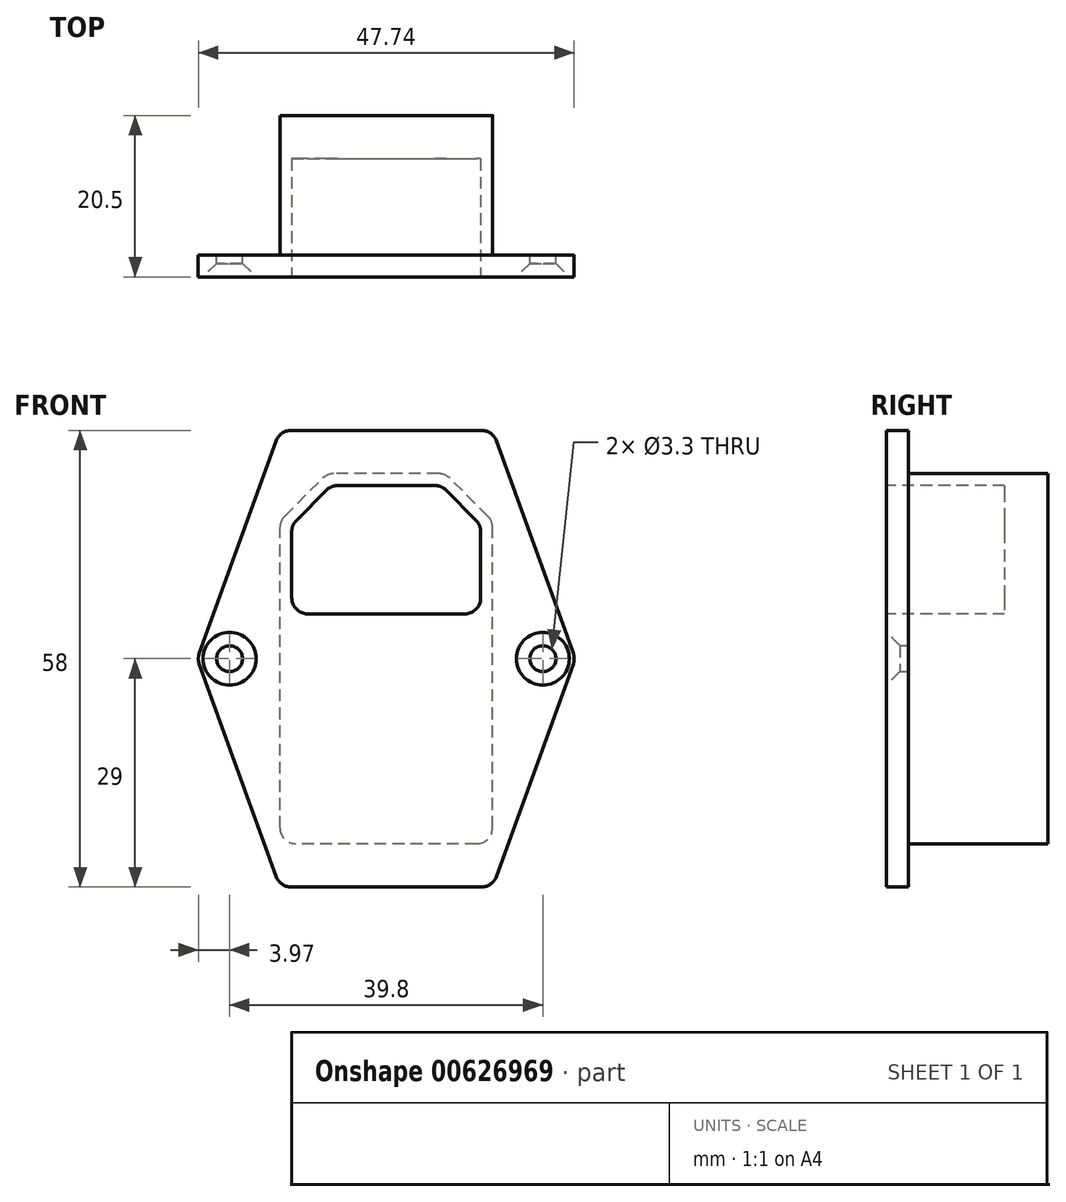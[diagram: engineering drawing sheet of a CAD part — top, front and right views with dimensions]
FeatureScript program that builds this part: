
annotation { "Feature Type Name" : "Feature", "Feature Type Description" : "" }
export const myFeature = defineFeature(function(context is Context, id is Id, definition is map)
    precondition{}
    {
        {
            var Q0;
            Q0=qCreatedBy(makeId("Front.planeOp"),FACE);
            var sketch = newSketch(context, id + "F0", { "sketchPlane" : qUnion([Q0])});
            skLineSegment(sketch, "E0", {"start": v(0, 0) * mm, "end": v(-13.5, 0) * mm});
            skLineSegment(sketch, "E1", {"start": v(-13.5, 0) * mm, "end": v(-13.5, 41) * mm});
            skLineSegment(sketch, "E2", {"start": v(-13.5, 41) * mm, "end": v(-7.5, 47) * mm});
            skLineSegment(sketch, "E3", {"start": v(-7.5, 47) * mm, "end": v(0, 47) * mm});
            skLineSegment(sketch, "E4", {"start": v(0, 47) * mm, "end": v(0, 0) * mm, "construction": true});
            skLineSegment(sketch, "E5", {"start": v(0, 23.5) * mm, "end": v(-24, 23.5) * mm, "construction": true});
            skLineSegment(sketch, "E6", {"start": v(0, 52.5) * mm, "end": v(-13.5, 52.5) * mm});
            skLineSegment(sketch, "E7", {"start": v(-13.5, 52.5) * mm, "end": v(-24, 23.5) * mm});
            skLineSegment(sketch, "E8.MirrorCS", {"start": v(0, -5.5) * mm, "end": v(-13.5, -5.5) * mm});
            skLineSegment(sketch, "E9.MirrorCS", {"start": v(-13.5, -5.5) * mm, "end": v(-24, 23.5) * mm});
            skLineSegment(sketch, "E10.MirrorCS", {"start": v(0, 52.5) * mm, "end": v(13.5, 52.5) * mm});
            skLineSegment(sketch, "E11.MirrorCS", {"start": v(13.5, 52.5) * mm, "end": v(24, 23.5) * mm});
            skLineSegment(sketch, "E12.MirrorCS", {"start": v(13.5, -5.5) * mm, "end": v(24, 23.5) * mm});
            skLineSegment(sketch, "E13.MirrorCS", {"start": v(0, -5.5) * mm, "end": v(13.5, -5.5) * mm});
            skLineSegment(sketch, "E14.MirrorCS", {"start": v(0, 0) * mm, "end": v(13.5, 0) * mm});
            skLineSegment(sketch, "E15.MirrorCS", {"start": v(7.5, 47) * mm, "end": v(0, 47) * mm});
            skLineSegment(sketch, "E16.MirrorCS", {"start": v(13.5, 41) * mm, "end": v(7.5, 47) * mm});
            skLineSegment(sketch, "E17.MirrorCS", {"start": v(13.5, 0) * mm, "end": v(13.5, 41) * mm});
            skSolve(sketch);
        }
        {
            var Q0;
            Q0=makeQuery(id+"F0.imprint","IMPRINT",FACE,{"disambiguationData":[TD([[makeQuery(id+"F0.imprint","IMPRINT",EDGE,{"derivedFrom":sQuery(id+"F0.wireOp",EDGE,"E0")}),1.0]])]});
            var Q1;
            Q1=makeQuery(id+"F0.imprint","IMPRINT",FACE,{"disambiguationData":[TD([[makeQuery(id+"F0.imprint","IMPRINT",EDGE,{"derivedFrom":sQuery(id+"F0.wireOp",EDGE,"E0")}),-1.0]])]});
            extrude(context, id + "F1", {"entities" : qUnion([Q0, Q1]), "depth" : 2.75 * mm, "offsetDistance" : 25 * mm});
        }
        {
            var Q0;
            Q0=makeQuery(id+"F0.imprint","IMPRINT",FACE,{"disambiguationData":[TD([[makeQuery(id+"F0.imprint","IMPRINT",EDGE,{"derivedFrom":sQuery(id+"F0.wireOp",EDGE,"E0")}),-1.0]])]});
            extrude(context, id + "F2", {"entities" : qUnion([Q0]), "operationType" : NewBodyOperationType.ADD, "oppositeDirection" : true, "depth" : (20.5 - 2.75) * mm, "offsetDistance" : 25 * mm});
        }
        {
            var Q0;
            Q0=makeQuery(id+"F1.opExtrude","CAP_FACE",FACE,{"disambiguationData":[OSD([sQuery(id+"F0.wireOp",EDGE,"E6"),sQuery(id+"F0.wireOp",EDGE,"E7"),sQuery(id+"F0.wireOp",EDGE,"E8.MirrorCS"),sQuery(id+"F0.wireOp",EDGE,"E9.MirrorCS"),sQuery(id+"F0.wireOp",EDGE,"E10.MirrorCS"),sQuery(id+"F0.wireOp",EDGE,"E11.MirrorCS"),sQuery(id+"F0.wireOp",EDGE,"E12.MirrorCS"),sQuery(id+"F0.wireOp",EDGE,"E13.MirrorCS")])],"isStart":false});
            var sketch = newSketch(context, id + "F3", { "sketchPlane" : qUnion([Q0])});
            skCircle(sketch, "E18", {"center": v(-19.9, 23.5) * mm, "radius": 1.9 * mm});
            skCircle(sketch, "E19.MirrorC", {"center": v(19.9, 23.5) * mm, "radius": 1.9 * mm});
            skSolve(sketch);
        }
        {
            var Q0;
            Q0=sQuery(id+"F3.wireOp",VERTEX,"E18.center");
            var Q1;
            Q1=sQuery(id+"F3.wireOp",VERTEX,"E19.MirrorC.center");
            var Q2;
            Q2=makeQuery(id+"F1.opExtrude","SWEPT_BODY",BODY,{"disambiguationData":[OSD([sQuery(id+"F0.wireOp",EDGE,"E6"),sQuery(id+"F0.wireOp",EDGE,"E7"),sQuery(id+"F0.wireOp",EDGE,"E8.MirrorCS"),sQuery(id+"F0.wireOp",EDGE,"E9.MirrorCS"),sQuery(id+"F0.wireOp",EDGE,"E10.MirrorCS"),sQuery(id+"F0.wireOp",EDGE,"E11.MirrorCS"),sQuery(id+"F0.wireOp",EDGE,"E12.MirrorCS"),sQuery(id+"F0.wireOp",EDGE,"E13.MirrorCS")])]});
            hole(context, id + "F4", {"style" : HoleStyle.C_SINK, "endStyle" : HoleEndStyle.THROUGH, "standardTappedOrClearance" : lookupTablePath({ "fit" : "Normal", "standard" : "ISO", "size" : "M3", "type" : "Clearance" }), "standardBlindInLast" : lookupTablePath({ "fit" : "Standard", "standard" : "ISO", "size" : "M3", "type" : "Clearance" }), "holeDiameter" : 3.3 * mm, "cSinkDiameter" : 6.72 * mm, "cSinkAngle" : 90 * degree, "majorDiameter" : 5 * mm, "isTappedThrough" : true, "tappedDepth" : 8.5 * mm, "tapClearance" : 3, "locations" : qUnion([Q0, Q1]), "scope" : qUnion([Q2]), "startStyle" : HoleStartStyle.PART});
        }
        {
            var Q0;
            Q0=makeQuery(id+"F1.opExtrude","CAP_FACE",FACE,{"disambiguationData":[OSD([sQuery(id+"F0.wireOp",EDGE,"E6"),sQuery(id+"F0.wireOp",EDGE,"E7"),sQuery(id+"F0.wireOp",EDGE,"E8.MirrorCS"),sQuery(id+"F0.wireOp",EDGE,"E9.MirrorCS"),sQuery(id+"F0.wireOp",EDGE,"E10.MirrorCS"),sQuery(id+"F0.wireOp",EDGE,"E11.MirrorCS"),sQuery(id+"F0.wireOp",EDGE,"E12.MirrorCS"),sQuery(id+"F0.wireOp",EDGE,"E13.MirrorCS")])],"isStart":false});
            var sketch = newSketch(context, id + "F5", { "sketchPlane" : qUnion([Q0])});
            skLineSegment(sketch, "E20", {"start": v(0, 52.5) * mm, "end": v(0, 0) * mm, "construction": true});
            skLineSegment(sketch, "E21", {"start": v(0, 45.5) * mm, "end": v(-7, 45.5) * mm});
            skLineSegment(sketch, "E22", {"start": v(-7, 45.5) * mm, "end": v(-12, 40.5) * mm});
            skLineSegment(sketch, "E23", {"start": v(-12, 40.5) * mm, "end": v(-12, 29.2) * mm});
            skLineSegment(sketch, "E24", {"start": v(-12, 29.2) * mm, "end": v(0, 29.2) * mm});
            skLineSegment(sketch, "E25", {"start": v(-8, 46.5) * mm, "end": v(-7, 45.5) * mm, "construction": true});
            skLineSegment(sketch, "E26.MirrorCS", {"start": v(0, 45.5) * mm, "end": v(7, 45.5) * mm});
            skLineSegment(sketch, "E27.MirrorCS", {"start": v(7, 45.5) * mm, "end": v(12, 40.5) * mm});
            skLineSegment(sketch, "E28.MirrorCS", {"start": v(12, 40.5) * mm, "end": v(12, 29.2) * mm});
            skLineSegment(sketch, "E29.MirrorCS", {"start": v(12, 29.2) * mm, "end": v(0, 29.2) * mm});
            skLineSegment(sketch, "E30.0", {"start": v(-13.5, 41) * mm, "end": v(-13, 41.5) * mm});
            skLineSegment(sketch, "E31", {"start": v(-12, 40.5) * mm, "end": v(-13, 41.5) * mm, "construction": true});
            skLineSegment(sketch, "E32", {"start": v(-13, 41.5) * mm, "end": v(-8, 46.5) * mm});
            skLineSegment(sketch, "E33", {"start": v(-8, 46.5) * mm, "end": v(-7.5, 47) * mm});
            skSolve(sketch);
        }
        {
            var Q0;
            Q0=makeQuery(id+"F5.imprint","IMPRINT",FACE,{"disambiguationData":[TD([[makeQuery(id+"F5.imprint","IMPRINT",EDGE,{"derivedFrom":sQuery(id+"F5.wireOp",EDGE,"E21")}),1.0]])]});
            extrude(context, id + "F6", {"entities" : qUnion([Q0]), "operationType" : NewBodyOperationType.REMOVE, "oppositeDirection" : true, "depth" : 15 * mm, "offsetDistance" : 25 * mm});
        }
        {
            var Q0;
            Q0=makeQuery(id+"F1.opExtrude","SWEPT_EDGE",EDGE,{"disambiguationData":[OSD([sQuery(id+"F0.wireOp",EDGE,"E10.MirrorCS"),sQuery(id+"F0.wireOp",EDGE,"E11.MirrorCS")])]});
            var Q1;
            Q1=makeQuery(id+"F1.opExtrude","SWEPT_EDGE",EDGE,{"disambiguationData":[OSD([sQuery(id+"F0.wireOp",EDGE,"E6"),sQuery(id+"F0.wireOp",EDGE,"E7")])]});
            var Q2;
            Q2=makeQuery(id+"F2.opExtrude","SWEPT_EDGE",EDGE,{"disambiguationData":[OSD([sQuery(id+"F0.wireOp",EDGE,"E2"),sQuery(id+"F0.wireOp",EDGE,"E3")])]});
            var Q3;
            Q3=makeQuery(id+"F2.opExtrude","SWEPT_EDGE",EDGE,{"disambiguationData":[OSD([sQuery(id+"F0.wireOp",EDGE,"E1"),sQuery(id+"F0.wireOp",EDGE,"E2")])]});
            var Q4;
            Q4=makeQuery(id+"F2.opExtrude","SWEPT_EDGE",EDGE,{"disambiguationData":[OSD([sQuery(id+"F0.wireOp",EDGE,"E15.MirrorCS"),sQuery(id+"F0.wireOp",EDGE,"E16.MirrorCS")])]});
            var Q5;
            Q5=makeQuery(id+"F2.opExtrude","SWEPT_EDGE",EDGE,{"disambiguationData":[OSD([sQuery(id+"F0.wireOp",EDGE,"E16.MirrorCS"),sQuery(id+"F0.wireOp",EDGE,"E17.MirrorCS")])]});
            var Q6;
            Q6=makeQuery(id+"F1.opExtrude","SWEPT_EDGE",EDGE,{"disambiguationData":[OSD([sQuery(id+"F0.wireOp",EDGE,"E7"),sQuery(id+"F0.wireOp",EDGE,"E9.MirrorCS")])]});
            var Q7;
            Q7=makeQuery(id+"F1.opExtrude","SWEPT_EDGE",EDGE,{"disambiguationData":[OSD([sQuery(id+"F0.wireOp",EDGE,"E8.MirrorCS"),sQuery(id+"F0.wireOp",EDGE,"E9.MirrorCS")])]});
            var Q8;
            Q8=makeQuery(id+"F1.opExtrude","SWEPT_EDGE",EDGE,{"disambiguationData":[OSD([sQuery(id+"F0.wireOp",EDGE,"E12.MirrorCS"),sQuery(id+"F0.wireOp",EDGE,"E13.MirrorCS")])]});
            var Q9;
            Q9=makeQuery(id+"F1.opExtrude","SWEPT_EDGE",EDGE,{"disambiguationData":[OSD([sQuery(id+"F0.wireOp",EDGE,"E11.MirrorCS"),sQuery(id+"F0.wireOp",EDGE,"E12.MirrorCS")])]});
            var Q10;
            Q10=makeQuery(id+"F2.opExtrude","SWEPT_EDGE",EDGE,{"disambiguationData":[OSD([sQuery(id+"F0.wireOp",EDGE,"E14.MirrorCS"),sQuery(id+"F0.wireOp",EDGE,"E17.MirrorCS")])]});
            var Q11;
            Q11=makeQuery(id+"F2.opExtrude","SWEPT_EDGE",EDGE,{"disambiguationData":[OSD([sQuery(id+"F0.wireOp",EDGE,"E0"),sQuery(id+"F0.wireOp",EDGE,"E1")])]});
            var Q12;
            Q12=makeQuery(id+"F6.boolean.opBoolean","COPY",EDGE,{"derivedFrom":makeQuery(id+"F6.opExtrude","SWEPT_EDGE",EDGE,{"disambiguationData":[OSD([sQuery(id+"F5.wireOp",EDGE,"E23"),sQuery(id+"F5.wireOp",EDGE,"E24")])]})});
            var Q13;
            Q13=makeQuery(id+"F6.boolean.opBoolean","COPY",EDGE,{"derivedFrom":makeQuery(id+"F6.opExtrude","SWEPT_EDGE",EDGE,{"disambiguationData":[OSD([sQuery(id+"F5.wireOp",EDGE,"E28.MirrorCS"),sQuery(id+"F5.wireOp",EDGE,"E29.MirrorCS")])]})});
            var Q14;
            Q14=makeQuery(id+"F6.boolean.opBoolean","COPY",EDGE,{"derivedFrom":makeQuery(id+"F6.opExtrude","SWEPT_EDGE",EDGE,{"disambiguationData":[OSD([sQuery(id+"F5.wireOp",EDGE,"E27.MirrorCS"),sQuery(id+"F5.wireOp",EDGE,"E28.MirrorCS")])]})});
            var Q15;
            Q15=makeQuery(id+"F6.boolean.opBoolean","COPY",EDGE,{"derivedFrom":makeQuery(id+"F6.opExtrude","SWEPT_EDGE",EDGE,{"disambiguationData":[OSD([sQuery(id+"F5.wireOp",EDGE,"E26.MirrorCS"),sQuery(id+"F5.wireOp",EDGE,"E27.MirrorCS")])]})});
            var Q16;
            Q16=makeQuery(id+"F6.boolean.opBoolean","COPY",EDGE,{"derivedFrom":makeQuery(id+"F6.opExtrude","SWEPT_EDGE",EDGE,{"disambiguationData":[OSD([sQuery(id+"F5.wireOp",EDGE,"E22"),sQuery(id+"F5.wireOp",EDGE,"E23")])]})});
            var Q17;
            Q17=makeQuery(id+"F6.boolean.opBoolean","COPY",EDGE,{"derivedFrom":makeQuery(id+"F6.opExtrude","SWEPT_EDGE",EDGE,{"disambiguationData":[OSD([sQuery(id+"F5.wireOp",EDGE,"E21"),sQuery(id+"F5.wireOp",EDGE,"E22")])]})});
            fillet(context, id + "F7", {"entities" : qUnion([Q0, Q1, Q2, Q3, Q4, Q5, Q6, Q7, Q8, Q9, Q10, Q11, Q12, Q13, Q14, Q15, Q16, Q17]), "radius" : 2 * mm, "tangentPropagation" : true, "allowEdgeOverflow" : false});
        }
    });
